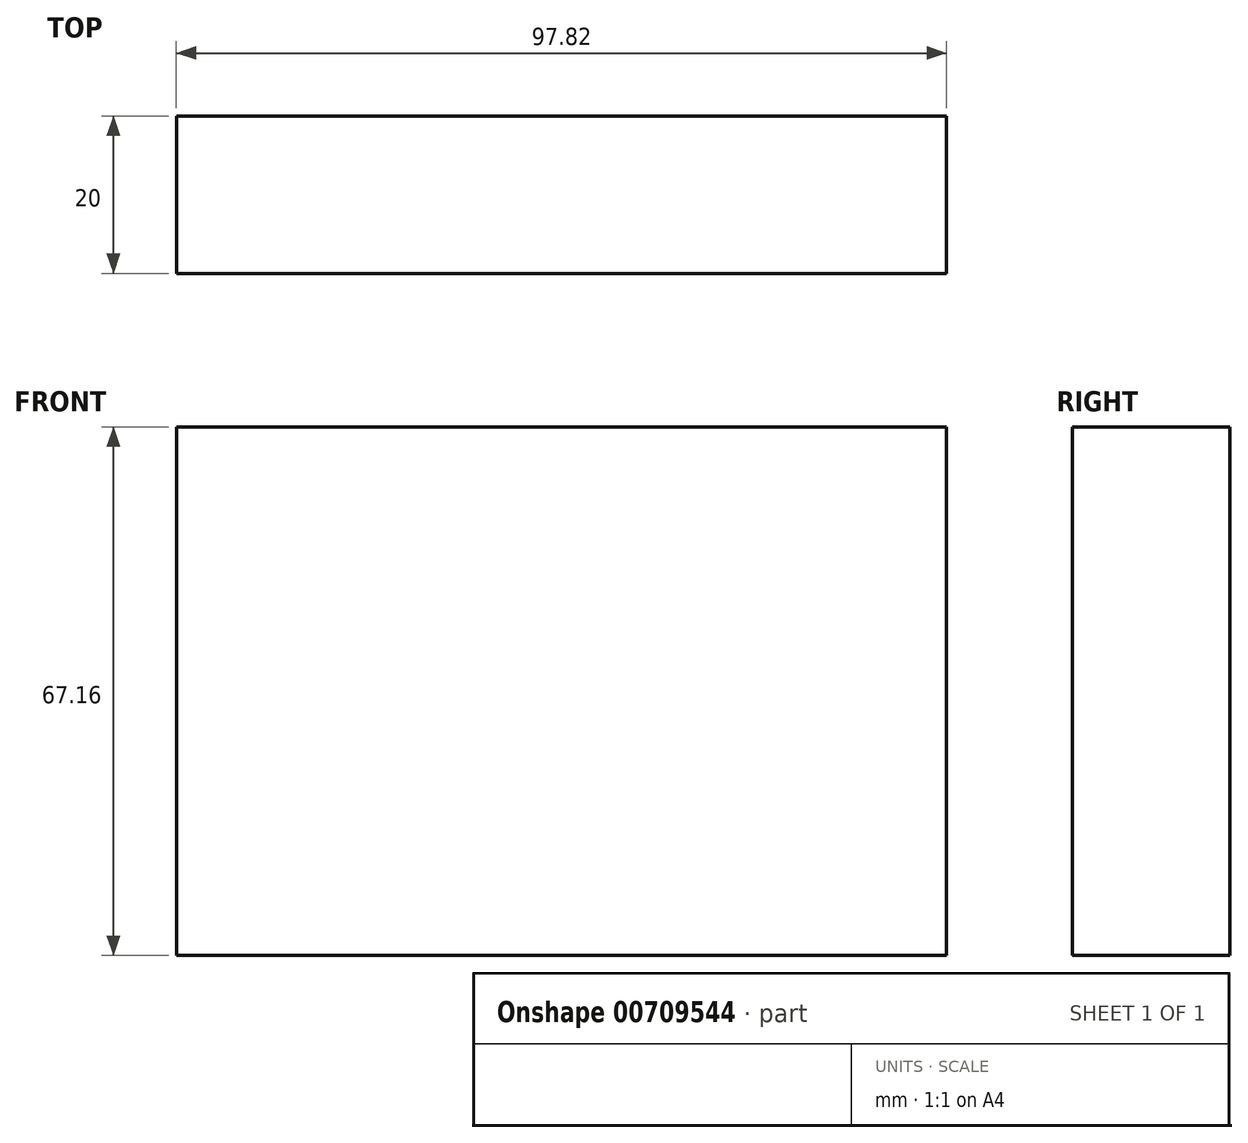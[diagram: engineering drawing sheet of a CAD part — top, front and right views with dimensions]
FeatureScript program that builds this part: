
annotation { "Feature Type Name" : "Feature", "Feature Type Description" : "" }
export const myFeature = defineFeature(function(context is Context, id is Id, definition is map)
    precondition{}
    {
        {
            var Q0;
            Q0=qCreatedBy(makeId("Front.planeOp"),FACE);
            var sketch = newSketch(context, id + "F0", { "sketchPlane" : qUnion([Q0])});
            skLineSegment(sketch, "E0.bottom", {"start": v(-38.4, 50.37) * mm, "end": v(59.42, 50.37) * mm});
            skLineSegment(sketch, "E0.top", {"start": v(-38.4, -16.8) * mm, "end": v(59.42, -16.8) * mm});
            skLineSegment(sketch, "E0.left", {"start": v(-38.4, 50.37) * mm, "end": v(-38.4, -16.8) * mm});
            skLineSegment(sketch, "E0.right", {"start": v(59.42, 50.37) * mm, "end": v(59.42, -16.8) * mm});
            skSolve(sketch);
        }
        {
            var Q0;
            Q0 = qSketchRegion(id + "F0", true);
            extrude(context, id + "F1", {"entities" : qUnion([Q0]), "depth" : 20 * mm, "offsetDistance" : 25.4 * mm});
        }
    });
